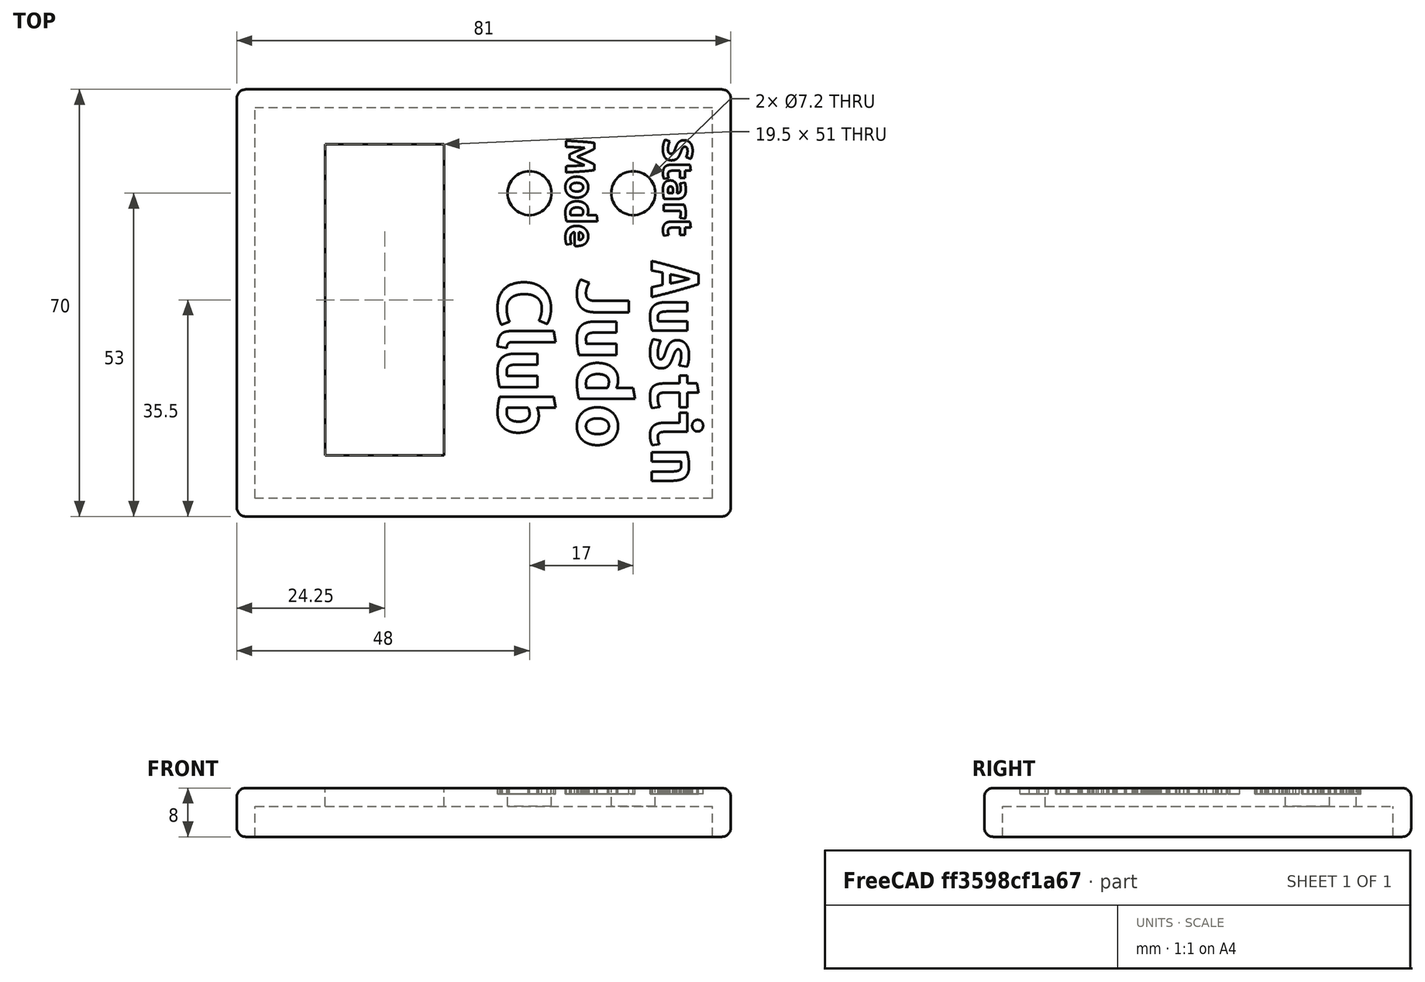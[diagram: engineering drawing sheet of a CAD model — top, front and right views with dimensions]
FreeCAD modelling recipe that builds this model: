
FCSTD DOCUMENT  (FreeCAD 0.19R)
Label: RoundTimer-lid
License: All rights reserved
LicenseURL: http://en.wikipedia.org/wiki/All_rights_reserved
objects: Part::MultiFuse×6, Part::Part2DObjectPython×5, Part::Extrusion×5, Part::Box×4, Part::Cylinder×4, Part::Cut×4, Part::Fillet×1
note: 29 computed .brp shape members not serialized (recipe doc carries the construction recipe); baked Part::Feature solids carry a one-line shape summary decoded from their .brp

FEATURE [Part::Box] Box001  label="Cube001"
  AttacherType = Attacher::AttachEngine3D
  Height = 6
  Length = 51
  Width = 28
FEATURE [Part::Box] Box002  label="Cube002"
  AttacherType = Attacher::AttachEngine3D
  Height = 7
  Length = 51
  Placement = pos=(0,1,6) rot=(0,0,1;0rad)
  Width = 19.5
FEATURE [Part::MultiFuse] Fusion001  label="LCD Display"
  Placement = pos=(-10,-8,23) rot=(0,0,1;1.5708rad)
  Shapes = -> [Box001,Box002]
FEATURE [Part::Cylinder] Cylinder001
  Angle = 360
  AttacherType = Attacher::AttachEngine3D
  Height = 19
  Radius = 4.65
FEATURE [Part::Cylinder] Cylinder002
  Angle = 360
  AttacherType = Attacher::AttachEngine3D
  Height = 6.7
  Placement = pos=(0,0,19) rot=(0,0,1;0rad)
  Radius = 3.6
FEATURE [Part::MultiFuse] Fusion002  label="Push Button mode/reset"
  Placement = pos=(20,35,12) rot=(1,0,0;0rad)
  Shapes = -> [Cylinder001,Cylinder002]
FEATURE [Part::Cylinder] Cylinder003
  Angle = 360
  AttacherType = Attacher::AttachEngine3D
  Height = 19
  Radius = 4.65
FEATURE [Part::Cylinder] Cylinder004
  Angle = 360
  AttacherType = Attacher::AttachEngine3D
  Height = 6.7
  Placement = pos=(0,0,19) rot=(0,0,1;0rad)
  Radius = 3.6
FEATURE [Part::MultiFuse] Fusion003  label="Push Button start/stop"
  Placement = pos=(3,35,12) rot=(1,0,0;0rad)
  Shapes = -> [Cylinder003,Cylinder004]
FEATURE [Part::Box] Box010  label="OuterBox"
  AttacherType = Attacher::AttachEngine3D
  Height = 36
  Length = 75
  Placement = pos=(-42,-15,-3) rot=(0,0,1;0rad)
  Width = 64
FEATURE [Part::Box] Box  label="Lid"
  AttacherType = Attacher::AttachEngine3D
  Height = 8
  Length = 81
  Placement = pos=(-45,-18,28) rot=(0,0,1;0rad)
  Width = 70
FEATURE [Part::MultiFuse] Fusion
  Shapes = -> [Fusion001,Fusion002,Fusion003]
FEATURE [Part::Part2DObjectPython] ShapeString  # Draft 2D object (typed FeaturePython)
  FontFile = <path>
  Placement = pos=(23,24,36) rot=(0,0,-1;1.5708rad)
  Size = 4
  String = Austin
  Tracking = 0
FEATURE [Part::Extrusion] Extrude  label="Austin"
  Base = -> ShapeString
  Dir = (0,0,1)
  DirMode = 0
  FaceMakerClass = Part::FaceMakerBullseye
  LengthFwd = 1
  LengthRev = 0
  Placement = pos=(0,0,-1) rot=(0,0,1;0rad)
  Solid = false
  Symmetric = false
FEATURE [Part::Part2DObjectPython] ShapeString001  # Draft 2D object (typed FeaturePython)
  FontFile = <path>
  Placement = pos=(11,21,36) rot=(0,0,-1;1.5708rad)
  Size = 4.5
  String = Judo
  Tracking = 0
FEATURE [Part::Part2DObjectPython] ShapeString002  # Draft 2D object (typed FeaturePython)
  FontFile = <path>
  Placement = pos=(-2,21,36) rot=(0,0,-1;1.5708rad)
  Size = 4.5
  String = Club
  Tracking = 0
FEATURE [Part::Extrusion] Extrude001  label="Judo"
  Base = -> ShapeString001
  Dir = (0,0,1)
  DirMode = 0
  FaceMakerClass = Part::FaceMakerBullseye
  LengthFwd = 1
  LengthRev = 0
  Placement = pos=(0,0,-1) rot=(0,0,1;0rad)
  Solid = false
  Symmetric = false
FEATURE [Part::Extrusion] Extrude002  label="Club"
  Base = -> ShapeString002
  Dir = (0,0,1)
  DirMode = 0
  FaceMakerClass = Part::FaceMakerBullseye
  LengthFwd = 1
  LengthRev = 0
  Placement = pos=(0,0,-1) rot=(0,0,1;0rad)
  Solid = false
  Symmetric = false
FEATURE [Part::MultiFuse] Fusion004
  Shapes = -> [Extrude,Extrude001,Extrude002]
FEATURE [Part::Part2DObjectPython] ShapeString003  # Draft 2D object (typed FeaturePython)
  FontFile = <path>
  Placement = pos=(25,42,36) rot=(0,0,-1;1.5708rad)
  Size = 2.5
  String = Start
  Tracking = 0
FEATURE [Part::Part2DObjectPython] ShapeString004  # Draft 2D object (typed FeaturePython)
  FontFile = <path>
  Placement = pos=(9,42,36) rot=(0,0,-1;1.5708rad)
  Size = 2.5
  String = Mode
  Tracking = 0
FEATURE [Part::Extrusion] Extrude003
  Base = -> ShapeString003
  Dir = (0,0,1)
  DirMode = 0
  FaceMakerClass = Part::FaceMakerBullseye
  LengthFwd = 1
  LengthRev = 0
  Placement = pos=(0,2,-1) rot=(0,0,1;0rad)
  Solid = false
  Symmetric = false
FEATURE [Part::Extrusion] Extrude004
  Base = -> ShapeString004
  Dir = (0,0,1)
  DirMode = 0
  FaceMakerClass = Part::FaceMakerBullseye
  LengthFwd = 1
  LengthRev = 0
  Placement = pos=(0,2,-1) rot=(0,0,1;0rad)
  Solid = false
  Symmetric = false
FEATURE [Part::MultiFuse] Fusion005
  Shapes = -> [Extrude003,Extrude004]
FEATURE [Part::Fillet] Fillet
  Base = -> Box
  Edges = 12 edges r=1.5: [Edge1,Edge2,Edge3,Edge4,Edge5,Edge6,Edge7,Edge8,Edge9,Edge10,Edge11,Edge12]
FEATURE [Part::Cut] Cut001  label="Lid001"
  Base = -> Fillet
  Tool = -> Fusion
FEATURE [Part::Cut] Cut002
  Base = -> Cut001
  Tool = -> Fusion004
FEATURE [Part::Cut] Cut003
  Base = -> Cut002
  Tool = -> Fusion005
FEATURE [Part::Cut] Cut  label="Lid002"
  Base = -> Cut003
  Tool = -> Box010
note: 5 file-system paths scrubbed to <path> (originals preserved in the JSON sidecar)
